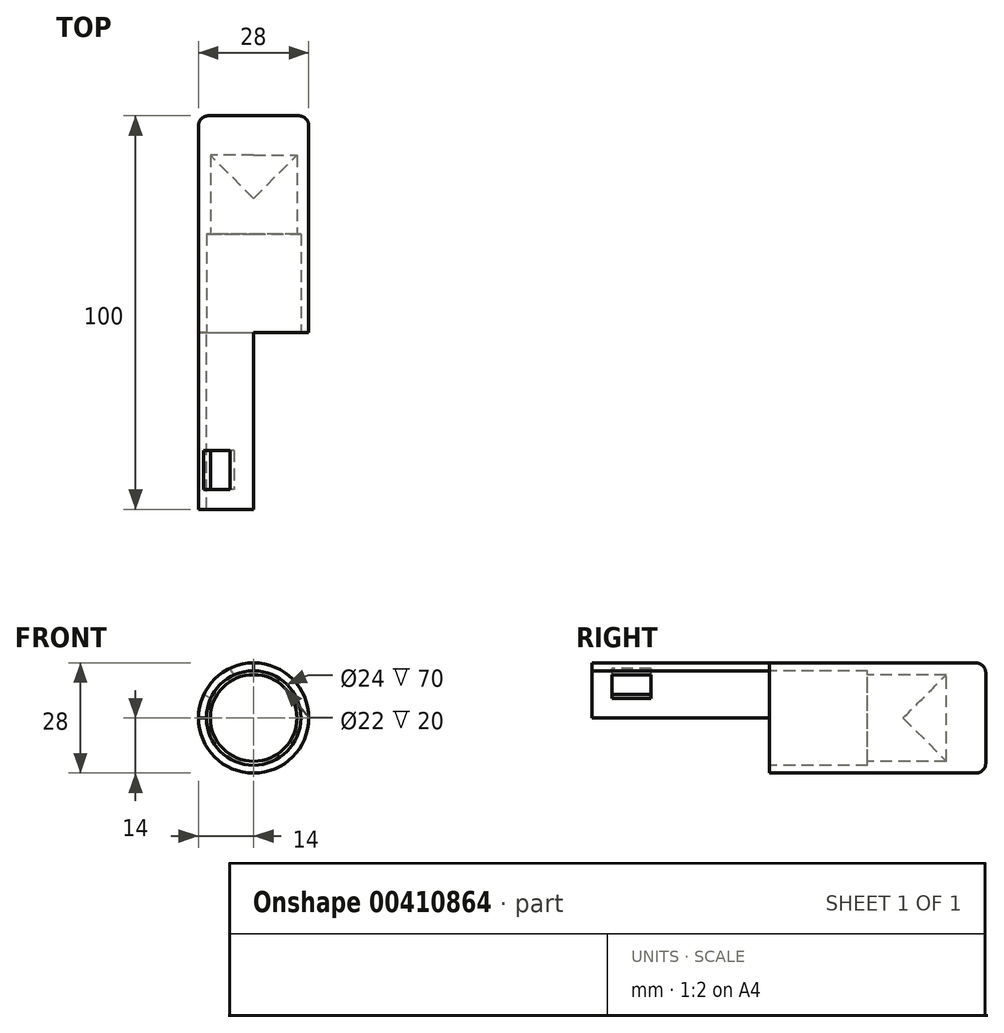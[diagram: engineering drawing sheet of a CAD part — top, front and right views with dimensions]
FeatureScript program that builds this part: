
annotation { "Feature Type Name" : "Feature", "Feature Type Description" : "" }
export const myFeature = defineFeature(function(context is Context, id is Id, definition is map)
    precondition{}
    {
        {
            var Q0;
            Q0=qCreatedBy(makeId("Front.planeOp"),FACE);
            var sketch = newSketch(context, id + "F0", { "sketchPlane" : qUnion([Q0])});
            skCircle(sketch, "E0", {"center": v(0, 0) * mm, "radius": 14 * mm});
            skSolve(sketch);
        }
        {
            var Q0;
            Q0=makeQuery(id+"F0.imprint","IMPRINT",FACE,{"disambiguationData":[TD([[makeQuery(id+"F0.imprint","IMPRINT",EDGE,{"derivedFrom":sQuery(id+"F0.wireOp",EDGE,"E0")}),1.0]])]});
            extrude(context, id + "F1", {"entities" : qUnion([Q0]), "depth" : 55 * mm});
        }
        {
            var Q0;
            Q0=makeQuery(id+"F1.opExtrude","CAP_FACE",FACE,{"disambiguationData":[OSD([sQuery(id+"F0.wireOp",EDGE,"E0")])],"isStart":false});
            var sketch = newSketch(context, id + "F2", { "sketchPlane" : qUnion([Q0])});
            skCircle(sketch, "E1", {"center": v(0, 0) * mm, "radius": 12 * mm});
            skSolve(sketch);
        }
        {
            var Q0;
            Q0=makeQuery(id+"F2.imprint","IMPRINT",FACE,{"disambiguationData":[TD([[makeQuery(id+"F2.imprint","IMPRINT",EDGE,{"derivedFrom":sQuery(id+"F2.wireOp",EDGE,"E1")}),1.0]])]});
            extrude(context, id + "F3", {"entities" : qUnion([Q0]), "operationType" : NewBodyOperationType.REMOVE, "oppositeDirection" : true, "depth" : 25 * mm});
        }
        {
            var Q0;
            Q0=makeQuery(id+"F3.boolean.opBoolean","COPY",FACE,{"derivedFrom":makeQuery(id+"F3.opExtrude","CAP_FACE",FACE,{"disambiguationData":[OSD([sQuery(id+"F2.wireOp",EDGE,"E1")])],"isStart":false})});
            var sketch = newSketch(context, id + "F4", { "sketchPlane" : qUnion([Q0])});
            skCircle(sketch, "E2", {"center": v(0, 0) * mm, "radius": 11 * mm});
            skSolve(sketch);
        }
        {
            var Q0;
            Q0=makeQuery(id+"F4.imprint","IMPRINT",FACE,{"disambiguationData":[TD([[makeQuery(id+"F4.imprint","IMPRINT",EDGE,{"derivedFrom":sQuery(id+"F4.wireOp",EDGE,"E2")}),1.0]])]});
            extrude(context, id + "F5", {"entities" : qUnion([Q0]), "operationType" : NewBodyOperationType.REMOVE, "oppositeDirection" : true, "depth" : 20 * mm});
        }
        {
            var Q0;
            Q0=makeQuery(id+"F1.opExtrude","CAP_EDGE",EDGE,{"disambiguationData":[OSD([sQuery(id+"F0.wireOp",EDGE,"E0")])],"isStart":true});
            fillet(context, id + "F6", {"entities" : qUnion([Q0]), "radius" : 2.5 * mm, "tangentPropagation" : true, "allowEdgeOverflow" : false});
        }
        {
            var Q0;
            Q0=qCreatedBy(makeId("Top.planeOp"),FACE);
            var sketch = newSketch(context, id + "F7", { "sketchPlane" : qUnion([Q0])});
            skLineSegment(sketch, "E3", {"start": v(0, -10) * mm, "end": v(0, -21) * mm});
            skLineSegment(sketch, "E4", {"start": v(0, -10) * mm, "end": v(-11, -10) * mm});
            skLineSegment(sketch, "E5", {"start": v(-11, -10) * mm, "end": v(0, -21) * mm});
            skSolve(sketch);
        }
        {
            var Q0;
            Q0 = qSketchRegion(id + "F7", true);
            var Q1;
            Q1=sQuery(id+"F7.wireOp",EDGE,"E3");
            revolve(context, id + "F8", {"operationType" : NewBodyOperationType.ADD, "entities" : qUnion([Q0]), "axis" : qUnion([Q1]), "revolveType" : RevolveType.FULL});
        }
        {
            var Q0;
            Q0=makeQuery(id+"F1.opExtrude","CAP_FACE",FACE,{"disambiguationData":[OSD([sQuery(id+"F0.wireOp",EDGE,"E0")])],"isStart":false});
            var sketch = newSketch(context, id + "F9", { "sketchPlane" : qUnion([Q0])});
            skLineSegment(sketch, "E6", {"start": v(-12, 0) * mm, "end": v(-14, 0) * mm});
            skLineSegment(sketch, "E7", {"start": v(0, 12) * mm, "end": v(0, 14) * mm});
            skSolve(sketch);
        }
        {
            var Q0;
            {var subQ0=sQuery(id+"F9.wireOp",EDGE,"E6");Q0=makeQuery(id+"F9.imprint","IMPRINT",FACE,{"disambiguationData":[TD([[makeQuery(id+"F9.imprint","IMPRINT",EDGE,{"derivedFrom":subQ0}),-1.0]])]});}
            extrude(context, id + "F10", {"entities" : qUnion([Q0]), "operationType" : NewBodyOperationType.ADD, "depth" : 45 * mm});
        }
        {
            var Q0;
            Q0=makeQuery(id+"F10.opExtrude","CAP_FACE",FACE,{"disambiguationData":[OSD([sQuery(id+"F0.wireOp",EDGE,"E0"),sQuery(id+"F2.wireOp",EDGE,"E1"),sQuery(id+"F9.wireOp",EDGE,"E6"),sQuery(id+"F9.wireOp",EDGE,"E7")])],"isStart":false});
            var sketch = newSketch(context, id + "F11", { "sketchPlane" : qUnion([Q0])});
            skLineSegment(sketch, "E8", {"start": v(-10.9, 5) * mm, "end": v(-12.65, 6) * mm});
            skLineSegment(sketch, "E9", {"start": v(-5, 10.9) * mm, "end": v(-6, 12.65) * mm});
            skSolve(sketch);
        }
        {
            var Q0;
            {var subQ0=sQuery(id+"F11.wireOp",EDGE,"E8");Q0=makeQuery(id+"F11.imprint","IMPRINT",FACE,{"disambiguationData":[TD([[makeQuery(id+"F11.imprint","IMPRINT",EDGE,{"derivedFrom":subQ0}),-1.0]])]});}
            extrude(context, id + "F12", {"entities" : qUnion([Q0]), "operationType" : NewBodyOperationType.REMOVE, "oppositeDirection" : true, "depth" : 15 * mm, "hasSecondDirection" : true, "secondDirectionOppositeDirection" : true, "secondDirectionDepth" : 5 * mm});
        }
    });
